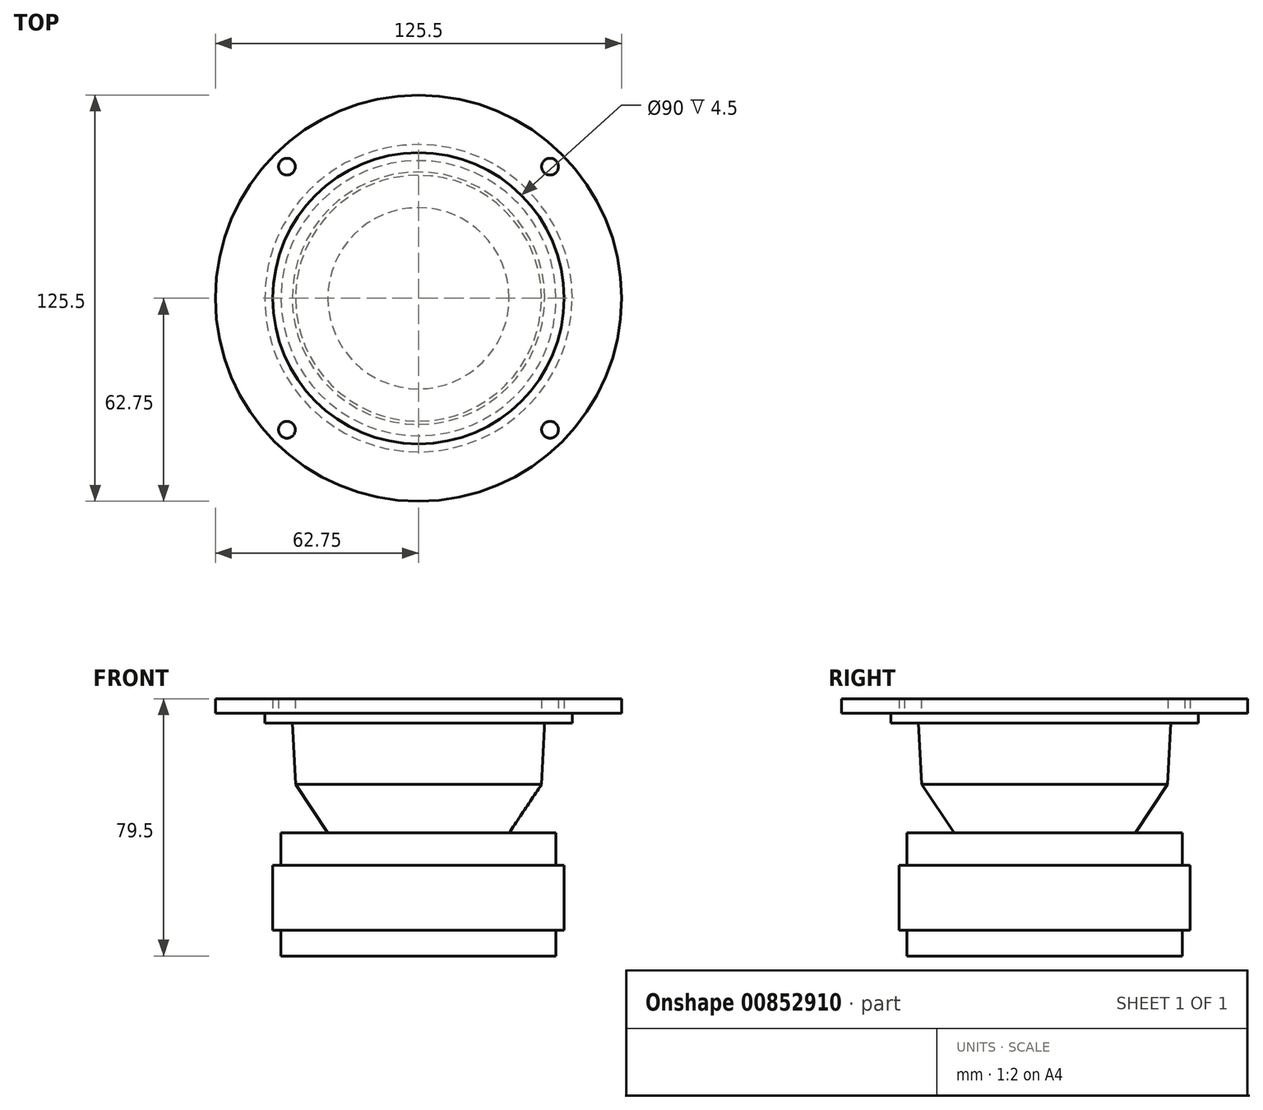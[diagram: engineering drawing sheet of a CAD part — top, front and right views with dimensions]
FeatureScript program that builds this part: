
annotation { "Feature Type Name" : "Feature", "Feature Type Description" : "" }
export const myFeature = defineFeature(function(context is Context, id is Id, definition is map)
    precondition{}
    {
        {
            var Q0;
            Q0=qCreatedBy(makeId("Right.planeOp"),FACE);
            var sketch = newSketch(context, id + "F0", { "sketchPlane" : qUnion([Q0])});
            skLineSegment(sketch, "E0.bottom", {"start": v(0, 0) * mm, "end": v(-62.75, 0) * mm});
            skLineSegment(sketch, "E0.top", {"start": v(0, 4.2) * mm, "end": v(-62.75, 4.2) * mm});
            skLineSegment(sketch, "E0.left", {"start": v(62.75, 0) * mm, "end": v(62.75, 4.2) * mm});
            skLineSegment(sketch, "E0.right", {"start": v(-62.75, 0) * mm, "end": v(-62.75, 4.2) * mm});
            skPoint(sketch, "E0.middle", {"position": v(0, 2.1) * mm});
            skLineSegment(sketch, "E1.bottom", {"start": v(-45, -47) * mm, "end": v(0, -47) * mm});
            skLineSegment(sketch, "E1.top", {"start": v(-45, -67) * mm, "end": v(0, -67) * mm});
            skLineSegment(sketch, "E1.left", {"start": v(-45, -47) * mm, "end": v(-45, -67) * mm});
            skPoint(sketch, "E1.middle", {"position": v(0, -57) * mm});
            skLineSegment(sketch, "E2.bottom", {"start": v(-42.5, -47) * mm, "end": v(0, -47) * mm});
            skLineSegment(sketch, "E2.top", {"start": v(-42.5, -37) * mm, "end": v(0, -37) * mm});
            skLineSegment(sketch, "E2.left", {"start": v(-42.5, -47) * mm, "end": v(-42.5, -37) * mm});
            skPoint(sketch, "E2.middle", {"position": v(0, -42) * mm});
            skLineSegment(sketch, "E3", {"start": v(-28, -37) * mm, "end": v(-38, -22) * mm});
            skLineSegment(sketch, "E4", {"start": v(-38, -22) * mm, "end": v(-39, -3) * mm});
            skLineSegment(sketch, "E5", {"start": v(-39, -3) * mm, "end": v(-47.5, -3) * mm});
            skLineSegment(sketch, "E6", {"start": v(-47.5, -3) * mm, "end": v(-47.5, 0) * mm});
            skLineSegment(sketch, "E7", {"start": v(0, 61.03) * mm, "end": v(0, -138.38) * mm, "construction": true});
            skLineSegment(sketch, "E8.bottom", {"start": v(-42.5, -67) * mm, "end": v(0, -67) * mm});
            skLineSegment(sketch, "E8.top", {"start": v(-42.5, -75) * mm, "end": v(0, -75) * mm});
            skLineSegment(sketch, "E8.left", {"start": v(-42.5, -67) * mm, "end": v(-42.5, -75) * mm});
            skPoint(sketch, "E8.middle", {"position": v(0, -71) * mm});
            skLineSegment(sketch, "E9", {"start": v(0, 0) * mm, "end": v(0, -75) * mm});
            skSolve(sketch);
        }
        {
            var Q0;
            Q0=qCreatedBy(makeId("Top.planeOp"),FACE);
            var sketch = newSketch(context, id + "F1", { "sketchPlane" : qUnion([Q0])});
            skCircle(sketch, "E10", {"center": v(0, 0) * mm, "radius": 57.5 * mm, "construction": true});
            skLineSegment(sketch, "E11", {"start": v(0, 0) * mm, "end": v(-40.66, -40.66) * mm, "construction": true});
            skCircle(sketch, "E12", {"center": v(-40.66, -40.66) * mm, "radius": 2.6 * mm});
            skLineSegment(sketch, "E13", {"start": v(-66.8, 0) * mm, "end": v(71.94, 0) * mm, "construction": true});
            skLineSegment(sketch, "E14", {"start": v(0, -68.55) * mm, "end": v(0, 71.6) * mm, "construction": true});
            skCircle(sketch, "E15.MirrorC", {"center": v(-40.66, 40.66) * mm, "radius": 2.6 * mm});
            skCircle(sketch, "E16.MirrorC", {"center": v(40.66, -40.66) * mm, "radius": 2.6 * mm});
            skCircle(sketch, "E17.MirrorC", {"center": v(40.66, 40.66) * mm, "radius": 2.6 * mm});
            skCircle(sketch, "E18", {"center": v(0, 0) * mm, "radius": 62.75 * mm});
            skPoint(sketch, "E19", {"position": v(0, -62.75) * mm});
            skCircle(sketch, "E20", {"center": v(0, 0) * mm, "radius": 45 * mm});
            skSolve(sketch);
        }
        {
            var Q0;
            Q0 = qSketchRegion(id + "F0", true);
            var Q1;
            Q1 = qConstructionFilter(qBodyType(qCreatedBy(id + "F0" ,EDGE), BodyType.WIRE), ConstructionObject.NO);
            var Q2;
            Q2=sQuery(id+"F0.wireOp",EDGE,"E7");
            revolve(context, id + "F2", {"surfaceOperationType" : NewSurfaceOperationType.NEW, "entities" : qUnion([Q0]), "surfaceEntities" : qUnion([Q1]), "axis" : qUnion([Q2]), "revolveType" : RevolveType.FULL});
        }
        {
            var Q0;
            Q0 = qSketchRegion(id + "F1", true);
            extrude(context, id + "F3", {"entities" : qUnion([Q0]), "operationType" : NewBodyOperationType.ADD, "depth" : 4.5 * mm, "offsetDistance" : 25 * mm});
        }
    });
